# Revit family: Table-LAMMHULTS-FUNK-Rectangle
name_source: partatom
category: Furniture
revit_build: Autodesk Revit Architecture 2012 (Build: 20110916_2132(x64)
units: mm (PartAtom-declared; Revit-internal decimal feet)

## types (1)
- THIS IS A CATALOG FAMILY
    Assembly Code = E2020
    Description = *Please enter mtrl description here for use in mto*
    Keynote = 46.B
    Leg Bar = No
    Leg Distance = 1000 mm  [stored 3.28084 ft]
    Leg Thickness = 35 mm  [stored 0.114829 ft]
    Leg Vault Height = 114 mm  [stored 0.374016 ft]
    Leg Width = 670 mm  [stored 2.19816 ft]
    Legs Material = Metal - White/Grey - Matte
    Manufacturer = LAMMHULTS
    Model = *Furniture model*
    Table Edge Material = Melamine - Stain - White/Grey
    Table Top Height = 450 mm  [stored 1.47638 ft]
    Table Top Length = 1600 mm  [stored 5.24934 ft]
    Table Top Material = Melamine - Stain - White/Grey
    Table Top Width = 800 mm  [stored 2.62467 ft]
    URL = www.lammhults.se

note: [stored X ft] marks values corroborated as IEEE doubles in the binary element streams (Revit-internal decimal feet)

## geometry (parser evidence)
native form markers: Blend x1, Sweep x1
no freeform markers — native parametric forms only
